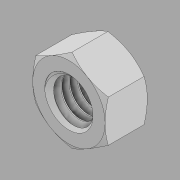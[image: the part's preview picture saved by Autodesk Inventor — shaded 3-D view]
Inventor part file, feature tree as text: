
AUTODESK INVENTOR PART (.ipt)
format: ipt  version: 2020 (Build 240168000, 168)  size: 304,640 bytes
history: native  units: in
note: dims shown in document units (in); Inventor stores cm internally (conversion verified against a paired STEP export)
features: mirror x1
ambient origin geometry x8: Origin, YZ Plane, XZ Plane, XY Plane, X Axis, Y Axis, Z Axis, Center Point
bodies: Solid1 (feature_tree)
feature tree (1):
  mirror  "Mirror1"
